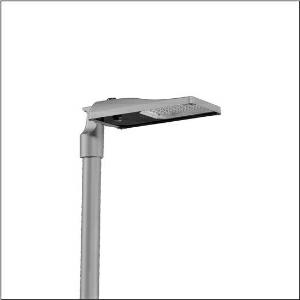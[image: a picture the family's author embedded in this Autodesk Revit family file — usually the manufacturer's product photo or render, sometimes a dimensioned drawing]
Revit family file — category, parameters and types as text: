
# Revit family: streetlight_sl_31_mini___p1_0a_5xh6a31t08ga_b1da
name_source: partatom
category: Lighting Fixtures
units: mm (PartAtom-declared; Revit-internal decimal feet)

## family parameters
Cut with Voids When Loaded = No
Host = Face
Light Source = No
Part Type = Normal
Room Calculation Point = No
Round Connector Dimension = Use Diameter
Shared = No

## types (1)
- --- (1 x LED, 5710 lm, 39.3 W, 3000K)
    Apparent Load = 39 VA
    CIE Flux Codes = 23 55 94 100 100
    Color Rendering = 70
    Color Temperature = 3000K
    Default Elevation = 1800 mm
    Description = Streetlight SL 31 mini D4i, Desk-Remote mast luminaire for post-top, side-entry; light control with lens of PMMA; light distribution: P1.0a, direct asymmetric distribution, for standard-compliant lighting for roads and squares; LED: luminous flux: 5.710lm, light colour: 730, colour temperature: 3000K; luminous efficacy: 145,3lm/W; control: pre-setting: logarithmic dimming characteristic, flexible luminous flux parameterisation, time-dependent luminous flux control, constant luminous flux control, power reduction, intelligent temperature release in ECG and LED module, overheat protection; luminaire housing, of diecast aluminium, SITECO metallic grey (DB 702S), corrosivity category C5 high according to DIN EN ISO 12944; cover of toughened safety glass, transparent, opened without tools; mast flange of diecast aluminium, SITECO metallic grey (DB 702S), spigot size: 76/60mm, mast flange included unmounted; with cable H07RN-F 2x 1.5mm², cable length: 6,5m, connection cable pre-assembled; mains connection: 220..240V, AC, 50/60Hz; power consumption (at start of service life): 39,3W / (at end of service life): 40,7W / (with reduced operation 50%): 18,1W; protection rating (complete): IP66; insulation class (complete): insulation class II (safety insulation); impact resistance: IK09; certification: CE, ENEC, ENEC+, VDE, UKCA, ZD4i; permissible operating ambient temperature for outdoor applications: -40..+50°C; packaging unit: 1 piece

Light Distribution: P1.0a
    Height = 76 mm
    Lamp = 1 x LED
    Lamp Light Flux = 5710 lm
    Lamp Power = 39.3 W
    Lamp count = 1
    Length = 547 mm
    Luminous efficacy = 145 lm/W
    Manufacturer = Siteco
    ModVariant = No
    Model = 5XH6A31T08GA
    Number of Poles = 1
    OnlyDefault = Yes
    Power Factor = 1
    Product Name = Streetlight SL 31 mini | P1.0a
    Product group = mast luminaire | pylon top
    ProductGroupID = 6100
    Protection Class = Protection class II
    Protection Degree = IP 66
    RLX_Detail_Level = 1
    RLX_Emergency_Light_Flux = 0 lm
    RLX_Emergency_Type = 0
    RLX_Emergency_Type_DB = No
    RlxData = <blob elided: 39661 chars, md5=1067498e>
    Socket = socket
    Standby Power = 0 W
    System Light Flux = 5710 lm
    System Power = 39 W
    Type Comments = factory setting: luminous flux: 100 % | dim-lin: 254 | 798 mA
    Type Image = l_1300332.jpg
    URL = http://relux.com
    VarID = @adj_064653
    Voltage = 0 V
    Weight = 0.00 kg
    Width = 265 mm

## geometry (parser evidence)
native form markers: Blend x4, Sweep x9
no freeform markers — native parametric forms only
